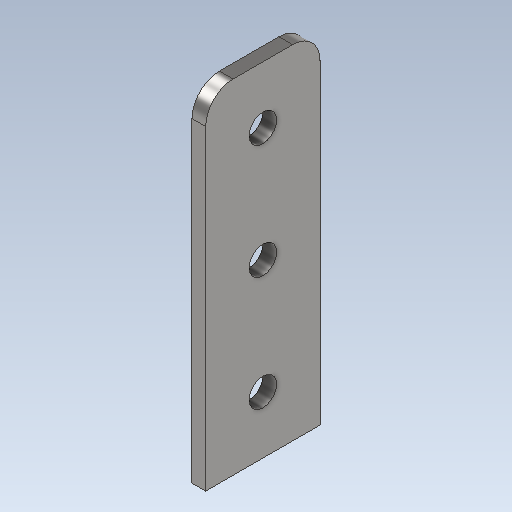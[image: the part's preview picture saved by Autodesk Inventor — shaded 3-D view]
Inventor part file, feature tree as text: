
AUTODESK INVENTOR PART (.ipt)
format: ipt  version: 2021 (Build 250183000, 183)  size: 124,416 bytes
history: native  units: mm
features: extrude x1, hole x1, fillet x1, sketch x1
ambient origin geometry x8: Origin, YZ Plane, XZ Plane, XY Plane, X Axis, Y Axis, Z Axis, Center Point
bodies: Solid1 (feature_tree)
feature tree (4):
  extrude  "Extrusion1"  Depth=50.0mm
  hole  "Hole2"  [1 undecoded]
  fillet  "Fillet3"  Radius=75.0mm
  sketch  "Sketch1"  dims[d0=150.0mm d1=50.0mm d2=25.0mm d3=75.0mm d4=6.0mm d5=0.0mm d15=50.0mm d16=50.0mm d17=12.0mm d18=6.0mm d19=4.0mm d20=2.0mm d21=90.0deg d22=8.0mm d23=20.594885mm d24=12.0mm]
note: 1 required parameter value undecoded (feature->parameter linkage not recoverable at this tier; creation-order binding heuristic only, values carry confidence <= 0.55)
